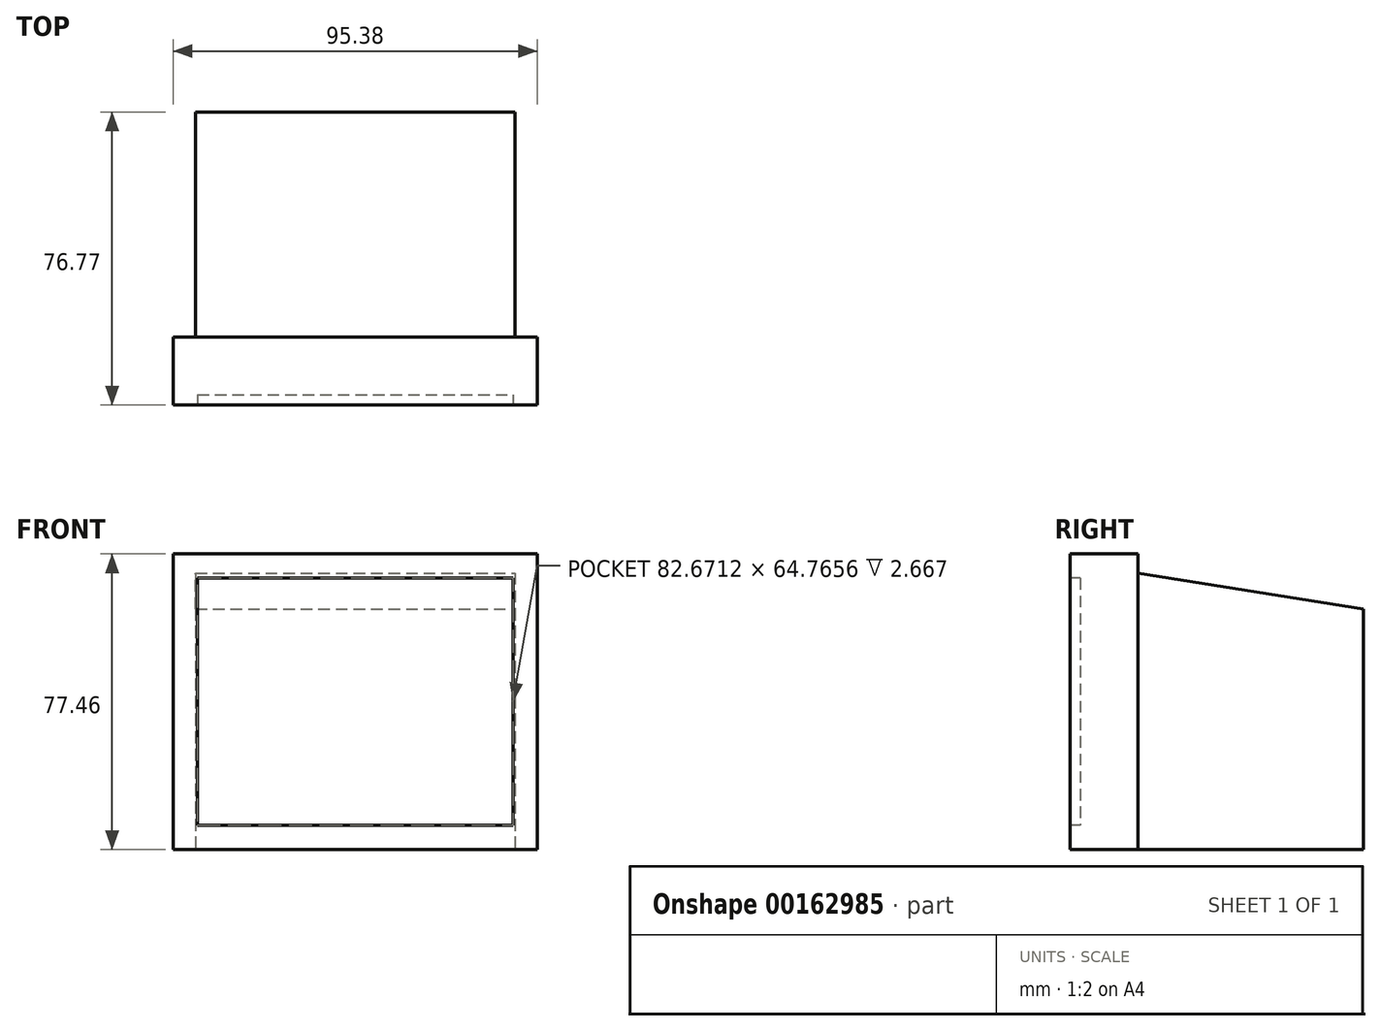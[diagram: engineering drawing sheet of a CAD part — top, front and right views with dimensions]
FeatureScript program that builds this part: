
annotation { "Feature Type Name" : "Feature", "Feature Type Description" : "" }
export const myFeature = defineFeature(function(context is Context, id is Id, definition is map)
    precondition{}
    {
        {
            var Q0;
            Q0=qCreatedBy(makeId("Front.planeOp"),FACE);
            var sketch = newSketch(context, id + "F0", { "sketchPlane" : qUnion([Q0])});
            skLineSegment(sketch, "E0.bottom", {"start": v(-47.69, 38.73) * mm, "end": v(47.69, 38.73) * mm});
            skLineSegment(sketch, "E0.top", {"start": v(-47.69, -38.73) * mm, "end": v(47.69, -38.73) * mm});
            skLineSegment(sketch, "E0.left", {"start": v(-47.69, 38.73) * mm, "end": v(-47.69, -38.73) * mm});
            skLineSegment(sketch, "E0.right", {"start": v(47.69, 38.73) * mm, "end": v(47.69, -38.73) * mm});
            skPoint(sketch, "E0.middle", {"position": v(0, 0) * mm});
            skSolve(sketch);
        }
        {
            var Q0;
            Q0=makeQuery(id+"F0.imprint","IMPRINT",FACE,{"disambiguationData":[TD([[makeQuery(id+"F0.imprint","IMPRINT",EDGE,{"derivedFrom":sQuery(id+"F0.wireOp",EDGE,"E0.bottom")}),-1.0]])]});
            extrude(context, id + "F1", {"entities" : qUnion([Q0]), "oppositeDirection" : true, "depth" : 10.16 * mm});
        }
        {
            var Q0;
            Q0=makeQuery(id+"F1.opExtrude","CAP_FACE",FACE,{"disambiguationData":[OSD([sQuery(id+"F0.wireOp",EDGE,"E0.bottom"),sQuery(id+"F0.wireOp",EDGE,"E0.top"),sQuery(id+"F0.wireOp",EDGE,"E0.left"),sQuery(id+"F0.wireOp",EDGE,"E0.right")])],"isStart":true});
            shell(context, id + "F2", {"entities" : qUnion([Q0]), "thickness" : 6.35 * mm});
        }
        {
            var Q0;
            Q0=makeQuery(id+"F2.opShell","OFFSET_FACE",FACE,{"disambiguationData":[OSD([sQuery(id+"F0.wireOp",EDGE,"E0.bottom"),sQuery(id+"F0.wireOp",EDGE,"E0.top"),sQuery(id+"F0.wireOp",EDGE,"E0.left"),sQuery(id+"F0.wireOp",EDGE,"E0.right")])]});
            extrude(context, id + "F3", {"entities" : qUnion([Q0]), "operationType" : NewBodyOperationType.ADD, "depth" : 5.6 * mm});
        }
        {
            var Q0;
            Q0=makeQuery(id+"F3.opExtrude","CAP_FACE",FACE,{"disambiguationData":[OSD([sQuery(id+"F0.wireOp",EDGE,"E0.bottom"),sQuery(id+"F0.wireOp",EDGE,"E0.top"),sQuery(id+"F0.wireOp",EDGE,"E0.left"),sQuery(id+"F0.wireOp",EDGE,"E0.right")])],"isStart":false});
            extrude(context, id + "F4", {"entities" : qUnion([Q0]), "operationType" : NewBodyOperationType.REMOVE, "oppositeDirection" : true, "depth" : 3.87 * mm});
        }
        {
            var Q0;
            Q0=makeQuery(id+"F4.boolean.opBoolean","COPY",FACE,{"derivedFrom":makeQuery(id+"F4.opExtrude","CAP_FACE",FACE,{"disambiguationData":[OSD([sQuery(id+"F0.wireOp",EDGE,"E0.bottom"),sQuery(id+"F0.wireOp",EDGE,"E0.top"),sQuery(id+"F0.wireOp",EDGE,"E0.left"),sQuery(id+"F0.wireOp",EDGE,"E0.right")])],"isStart":false})});
            extrude(context, id + "F5", {"entities" : qUnion([Q0]), "operationType" : NewBodyOperationType.REMOVE, "oppositeDirection" : true, "depth" : 0.57 * mm});
        }
        {
            var Q0;
            Q0=makeQuery(id+"F1.opExtrude","CAP_FACE",FACE,{"disambiguationData":[OSD([sQuery(id+"F0.wireOp",EDGE,"E0.bottom"),sQuery(id+"F0.wireOp",EDGE,"E0.top"),sQuery(id+"F0.wireOp",EDGE,"E0.left"),sQuery(id+"F0.wireOp",EDGE,"E0.right")])],"isStart":false});
            extrude(context, id + "F6", {"entities" : qUnion([Q0]), "operationType" : NewBodyOperationType.ADD, "depth" : 7.62 * mm});
        }
        {
            var Q0;
            Q0=makeQuery(id+"F6.opExtrude","CAP_FACE",FACE,{"disambiguationData":[OSD([sQuery(id+"F0.wireOp",EDGE,"E0.bottom"),sQuery(id+"F0.wireOp",EDGE,"E0.top"),sQuery(id+"F0.wireOp",EDGE,"E0.left"),sQuery(id+"F0.wireOp",EDGE,"E0.right")])],"isStart":false});
            var sketch = newSketch(context, id + "F7", { "sketchPlane" : qUnion([Q0])});
            skLineSegment(sketch, "E1.bottom", {"start": v(-41.84, 28.74) * mm, "end": v(41.84, 28.74) * mm});
            skLineSegment(sketch, "E1.top", {"start": v(-41.84, -28.74) * mm, "end": v(41.84, -28.74) * mm});
            skLineSegment(sketch, "E1.left", {"start": v(-41.84, 28.74) * mm, "end": v(-41.84, -28.74) * mm});
            skLineSegment(sketch, "E1.right", {"start": v(41.84, 28.74) * mm, "end": v(41.84, -28.74) * mm});
            skPoint(sketch, "E1.middle", {"position": v(0, 0) * mm});
            skLineSegment(sketch, "E2", {"start": v(-41.84, -28.74) * mm, "end": v(-41.84, -38.73) * mm});
            skLineSegment(sketch, "E3", {"start": v(-41.84, -38.73) * mm, "end": v(41.84, -38.73) * mm});
            skLineSegment(sketch, "E4", {"start": v(41.84, -38.73) * mm, "end": v(41.84, -28.74) * mm});
            skSolve(sketch);
        }
        {
            var Q0;
            Q0=makeQuery(id+"F7.imprint","IMPRINT",FACE,{"disambiguationData":[TD([[makeQuery(id+"F7.imprint","IMPRINT",EDGE,{"derivedFrom":sQuery(id+"F7.wireOp",EDGE,"E1.bottom")}),-1.0]])]});
            var Q1;
            Q1=makeQuery(id+"F7.imprint","IMPRINT",FACE,{"disambiguationData":[TD([[makeQuery(id+"F7.imprint","IMPRINT",EDGE,{"derivedFrom":sQuery(id+"F7.wireOp",EDGE,"E1.top")}),-1.0]])]});
            extrude(context, id + "F8", {"entities" : qUnion([Q0, Q1]), "operationType" : NewBodyOperationType.ADD, "depth" : 59 * mm});
        }
        {
            var Q0;
            Q0=makeQuery(id+"F8.opExtrude","SWEPT_FACE",FACE,{"disambiguationData":[OSD([sQuery(id+"F7.wireOp",EDGE,"E1.bottom")])]});
            extrude(context, id + "F9", {"entities" : qUnion([Q0]), "operationType" : NewBodyOperationType.ADD, "depth" : 5.7 * mm});
        }
        {
            var Q0;
            {var subQ0=sQuery(id+"F7.wireOp",EDGE,"E1.bottom");Q0=makeQuery(id+"F9.opExtrude","CAP_EDGE",EDGE,{"disambiguationData":[OSD([subQ0]),TDD([makeQuery(id+"F8.opExtrude","CAP_EDGE",EDGE,{"disambiguationData":[OSD([subQ0])],"isStart":false})])],"isStart":false});}
            chamfer(context, id + "F10", {"entities" : qUnion([Q0]), "chamferType" : ChamferType.TWO_OFFSETS, "width1" : 63.5 * mm, "oppositeDirection" : false, "width2" : 10.16 * mm, "tangentPropagation" : true});
        }
    });
